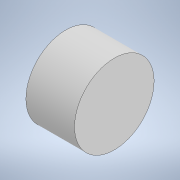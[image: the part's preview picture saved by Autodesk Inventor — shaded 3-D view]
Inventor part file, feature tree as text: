
AUTODESK INVENTOR PART (.ipt)
format: ipt  version: 2020 (Build 240168000, 168)  size: 110,080 bytes
history: native  units: in
note: dims shown in document units (in); Inventor stores cm internally (conversion verified against a paired STEP export)
features: extrude x2, sketch x2
ambient origin geometry x8: Origin, YZ Plane, XZ Plane, XY Plane, X Axis, Y Axis, Z Axis, Center Point
bodies: Solid1 (feature_tree)
feature tree (4):
  extrude  "Extrusion1"  Depth=0.1575in
  extrude  "Extrusion2"  Depth=0.2756in
  sketch  "Sketch1"  dims[d0=0.7087in d1=0.1575in]
  sketch  "Sketch2"  dims[d2=0.0in d4=0.2756in d5=0.0in]
